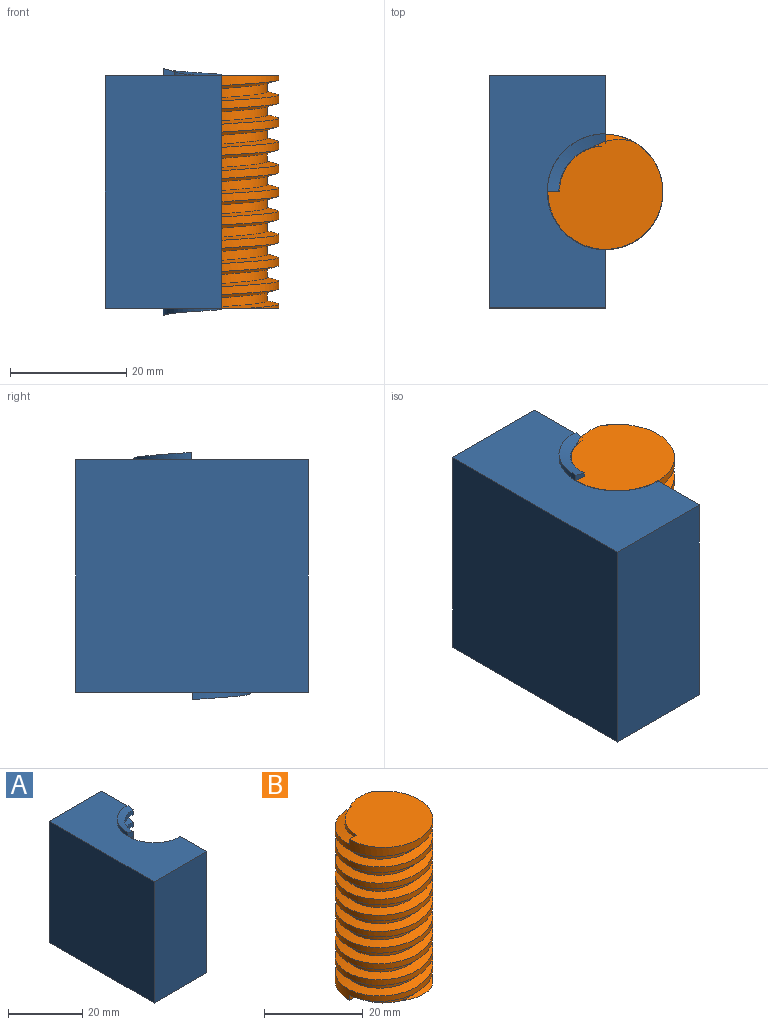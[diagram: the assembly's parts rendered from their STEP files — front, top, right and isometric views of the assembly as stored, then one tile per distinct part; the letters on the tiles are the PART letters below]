
ASSEMBLY  parts=2 mates=1
PART A: 54 faces, bbox 25x40x42.5 mm
  f0: cylinder r=10mm len=20mm, axis (0,0,-1), area 46mm2, adj f19,f30,f52,f53
  f1: cylinder r=10mm len=20mm, axis (0,0,-1), area 46mm2, adj f20,f31,f52,f53
  f2: cylinder r=10mm len=20mm, axis (0,0,-1), area 46mm2, adj f21,f32,f52,f53
  f3: cylinder r=10mm len=20mm, axis (0,0,-1), area 46mm2, adj f22,f33,f52,f53
  f4: cylinder r=10mm len=20mm, axis (0,0,-1), area 46mm2, adj f23,f34,f52,f53
  f5: cylinder r=10mm len=20mm, axis (0,0,-1), area 46mm2, adj f24,f35,f52,f53
  f6: cylinder r=10mm len=20mm, axis (0,0,-1), area 46mm2, adj f25,f36,f52,f53
  f7: cylinder r=10mm len=20mm, axis (0,0,-1), area 46mm2, adj f26,f37,f52,f53
  f8: cylinder r=10mm len=20mm, axis (0,0,-1), area 58.1mm2, adj f27,f38,f43,f47,f52,f53
  f9: cylinder r=8mm len=16mm, axis (0,0,1), area 36.8mm2, adj f27,f37,f52,f53
  f10: cylinder r=8mm len=16mm, axis (0,0,1), area 36.8mm2, adj f26,f36,f52,f53
  f11: cylinder r=8mm len=16mm, axis (0,0,1), area 36.8mm2, adj f25,f35,f52,f53
  f12: cylinder r=8mm len=16mm, axis (0,0,1), area 36.8mm2, adj f24,f34,f52,f53
  f13: cylinder r=8mm len=16mm, axis (0,0,1), area 36.8mm2, adj f23,f33,f52,f53
  f14: cylinder r=8mm len=16mm, axis (0,0,1), area 36.8mm2, adj f22,f32,f52,f53
  f15: cylinder r=8mm len=16mm, axis (0,0,1), area 36.8mm2, adj f21,f31,f52,f53
  f16: cylinder r=8mm len=16mm, axis (0,0,1), area 36.8mm2, adj f20,f30,f52,f53
  f17: cylinder r=8mm len=16mm, axis (0,0,1), area 36.8mm2, adj f19,f29,f52,f53
  f18: cylinder r=8mm len=8mm, axis (0,0,1), area 18.4mm2, adj f46,f49,f51,f52
  f19: bspline ~23.09x15mm, area 58.7mm2, adj f0,f17,f52,f53
  f20: bspline ~23.09x15mm, area 58.7mm2, adj f1,f16,f52,f53
  f21: bspline ~23.09x15mm, area 58.7mm2, adj f2,f15,f52,f53
  f22: bspline ~23.09x15mm, area 58.7mm2, adj f3,f14,f52,f53
  f23: bspline ~23.09x15mm, area 58.7mm2, adj f4,f13,f52,f53
  f24: bspline ~23.09x15mm, area 58.7mm2, adj f5,f12,f52,f53
  f25: bspline ~23.09x15mm, area 58.7mm2, adj f6,f11,f52,f53
  f26: bspline ~23.09x15mm, area 58.7mm2, adj f7,f10,f52,f53
  f27: bspline ~23.09x15mm, area 58.7mm2, adj f8,f9,f52,f53
  f28: bspline ~15x11.55mm, area 29.3mm2, adj f47,f48,f50,f53
  f29: bspline ~23.09x15mm, area 58.7mm2, adj f17,f39,f52,f53
  f30: bspline ~23.09x15mm, area 58.7mm2, adj f0,f16,f52,f53
  f31: bspline ~23.09x15mm, area 58.7mm2, adj f1,f15,f52,f53
  f32: bspline ~23.09x15mm, area 58.7mm2, adj f2,f14,f52,f53
  f33: bspline ~23.09x15mm, area 58.7mm2, adj f3,f13,f52,f53
  f34: bspline ~23.09x15mm, area 58.7mm2, adj f4,f12,f52,f53
  f35: bspline ~23.09x15mm, area 58.7mm2, adj f5,f11,f52,f53
  f36: bspline ~23.09x15mm, area 58.7mm2, adj f6,f10,f52,f53
  f37: bspline ~23.09x15mm, area 58.7mm2, adj f7,f9,f52,f53
  f38: bspline ~15x11.55mm, area 29.3mm2, adj f8,f47,f48,f53
  f39: cylinder r=10mm len=20mm, axis (0,0,-1), area 58.1mm2, adj f29,f44,f46,f49,f52,f53
  f40: plane 40x20mm, normal (0,1,0), area 800mm2, adj f41,f43,f44,f53
  f41: plane 40x40mm, normal (-1,0,0), area 1600mm2, adj f40,f42,f43,f44
  f42: plane 40x20mm, normal (0,-1,0), area 800mm2, adj f41,f43,f44,f52
  f43: plane 40x20mm, normal (0,0,1), area 642.9mm2, adj f8,f40,f41,f42,f50,f52,f53
  f44: plane 40x20mm, normal (0,0,-1), area 642.9mm2, adj f39,f40,f41,f42,f45,f52,f53
  f45: cylinder r=10mm len=10mm, axis (0,0,1), area 12.1mm2, adj f44,f46,f51,f52
  f46: plane 2.54x2mm, normal (0,1,0), area 4mm2, adj f18,f39,f45,f49,f51
  f47: plane 2.54x2mm, normal (0,-1,0), area 4mm2, adj f8,f28,f38,f48,f50
  f48: cylinder r=8mm len=8mm, axis (0,0,1), area 18.4mm2, adj f28,f38,f47,f53
  f49: bspline ~15x11.55mm, area 29.3mm2, adj f18,f39,f46,f52
  f50: cylinder r=10mm len=10mm, axis (0,0,1), area 12.1mm2, adj f28,f43,f47,f53
  f51: bspline ~15x11.55mm, area 29.3mm2, adj f18,f45,f46,f52
  f52: plane 40.27x12mm, normal (1,0,0), area 440mm2, adj f0,f1,f2,f3,f4,f5,f6,f7
  f53: plane 40.27x12mm, normal (1,0,0), area 440mm2, adj f0,f1,f2,f3,f4,f5,f6,f7
PART B: 8 faces, bbox 19.8x22.9x41.3 mm
  f0: cylinder r=9.9mm len=40mm, axis (0,0,-1), area 861.9mm2, adj f1,f2,f3,f5,f6,f7
  f1: plane 19.8x18.94mm, normal (0,0,-1), area 278.3mm2, adj f0,f3,f4,f5
  f2: plane 19.8x18.94mm, normal (0,0,1), area 278.3mm2, adj f0,f4,f6,f7
  f3: plane 2x1.32mm, normal (0,-1,0), area 2.1mm2, adj f0,f1,f4,f7
  f4: cylinder r=7.9mm len=40mm, axis (0,0,1), area 708.3mm2, adj f1,f2,f3,f5,f6,f7
  f5: bspline ~39.87x22.86mm, area 1127.7mm2, adj f0,f1,f4,f6
  f6: plane 2x1.32mm, normal (0,1,0), area 2.1mm2, adj f0,f2,f4,f5
  f7: bspline ~39.87x22.86mm, area 1125.6mm2, adj f0,f2,f3,f4
PLACE A t=(-5.33,6.94,-4.97)mm fixed
PLACE B rot(axis=(0,0,-1),0.7deg) t=(-5.33,6.94,-4.97)mm
MATE cylindrical A.f0 <-> B.f0  axis (0,0,-1) through (-5.33,6.94,-4.97)mm
